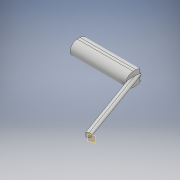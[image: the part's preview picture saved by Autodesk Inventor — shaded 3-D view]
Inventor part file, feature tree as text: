
AUTODESK INVENTOR PART (.ipt)
format: ipt  version: 2018.1 (Build 221171000, 171)  size: 145,920 bytes
history: native  units: mm
features: extrude x3, sketch x3, fillet x2, other x1
ambient origin geometry x8: Origin, YZ Plane, XZ Plane, XY Plane, X Axis, Y Axis, Z Axis, Center Point
bodies: Solide1 (feature_tree)
feature tree (9):
  extrude  "Extrusion1"  Depth=200.0mm
  fillet  "Congé1"  Radius=60.0mm
  other  "Plan de construction2"
  extrude  "Extrusion3"  Depth=100.0mm
  extrude  "Extrusion4"  Depth=30.0mm
  fillet  "Congé2"  Radius=50.0mm
  sketch  "Esquisse1"
  sketch  "Esquisse5"
  sketch  "Esquisse6"
